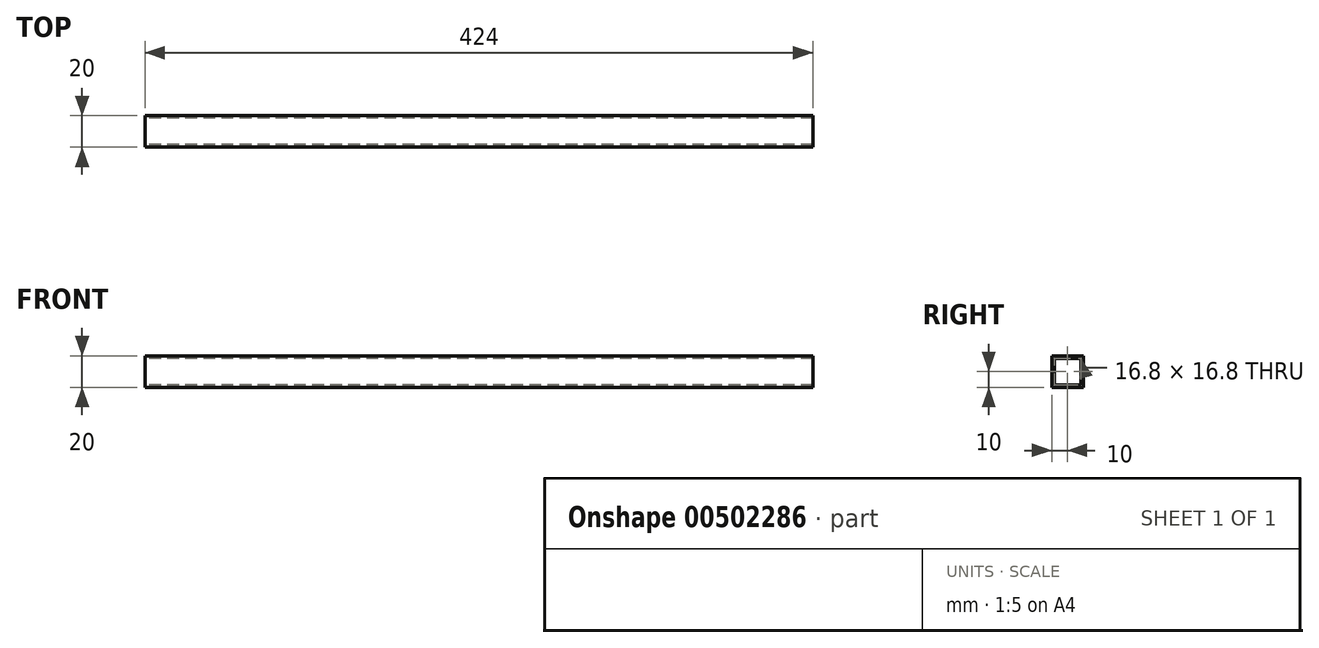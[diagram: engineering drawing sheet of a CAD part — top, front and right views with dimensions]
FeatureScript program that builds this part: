
annotation { "Feature Type Name" : "Feature", "Feature Type Description" : "" }
export const myFeature = defineFeature(function(context is Context, id is Id, definition is map)
    precondition{}
    {
        {
            var Q0;
            Q0=qCreatedBy(makeId("Right.planeOp"),FACE);
            var sketch = newSketch(context, id + "F0", { "sketchPlane" : qUnion([Q0])});
            skLineSegment(sketch, "E0.bottom", {"start": v(0, 0) * mm, "end": v(20, 0) * mm});
            skLineSegment(sketch, "E0.top", {"start": v(0, -20) * mm, "end": v(20, -20) * mm});
            skLineSegment(sketch, "E0.left", {"start": v(0, 0) * mm, "end": v(0, -20) * mm});
            skLineSegment(sketch, "E0.right", {"start": v(20, 0) * mm, "end": v(20, -20) * mm});
            skLineSegment(sketch, "E1.0", {"start": v(1.6, -1.6) * mm, "end": v(1.6, -18.4) * mm});
            skLineSegment(sketch, "E1.1", {"start": v(1.6, -1.6) * mm, "end": v(18.4, -1.6) * mm});
            skLineSegment(sketch, "E1.2", {"start": v(18.4, -1.6) * mm, "end": v(18.4, -18.4) * mm});
            skLineSegment(sketch, "E2", {"start": v(1.6, -18.4) * mm, "end": v(18.4, -18.4) * mm});
            skSolve(sketch);
        }
        {
            var Q0;
            Q0 = qSketchRegion(id + "F0", true);
            extrude(context, id + "F1", {"entities" : qUnion([Q0]), "endBound" : BoundingType.SYMMETRIC, "depth" : 424 * mm});
        }
    });
